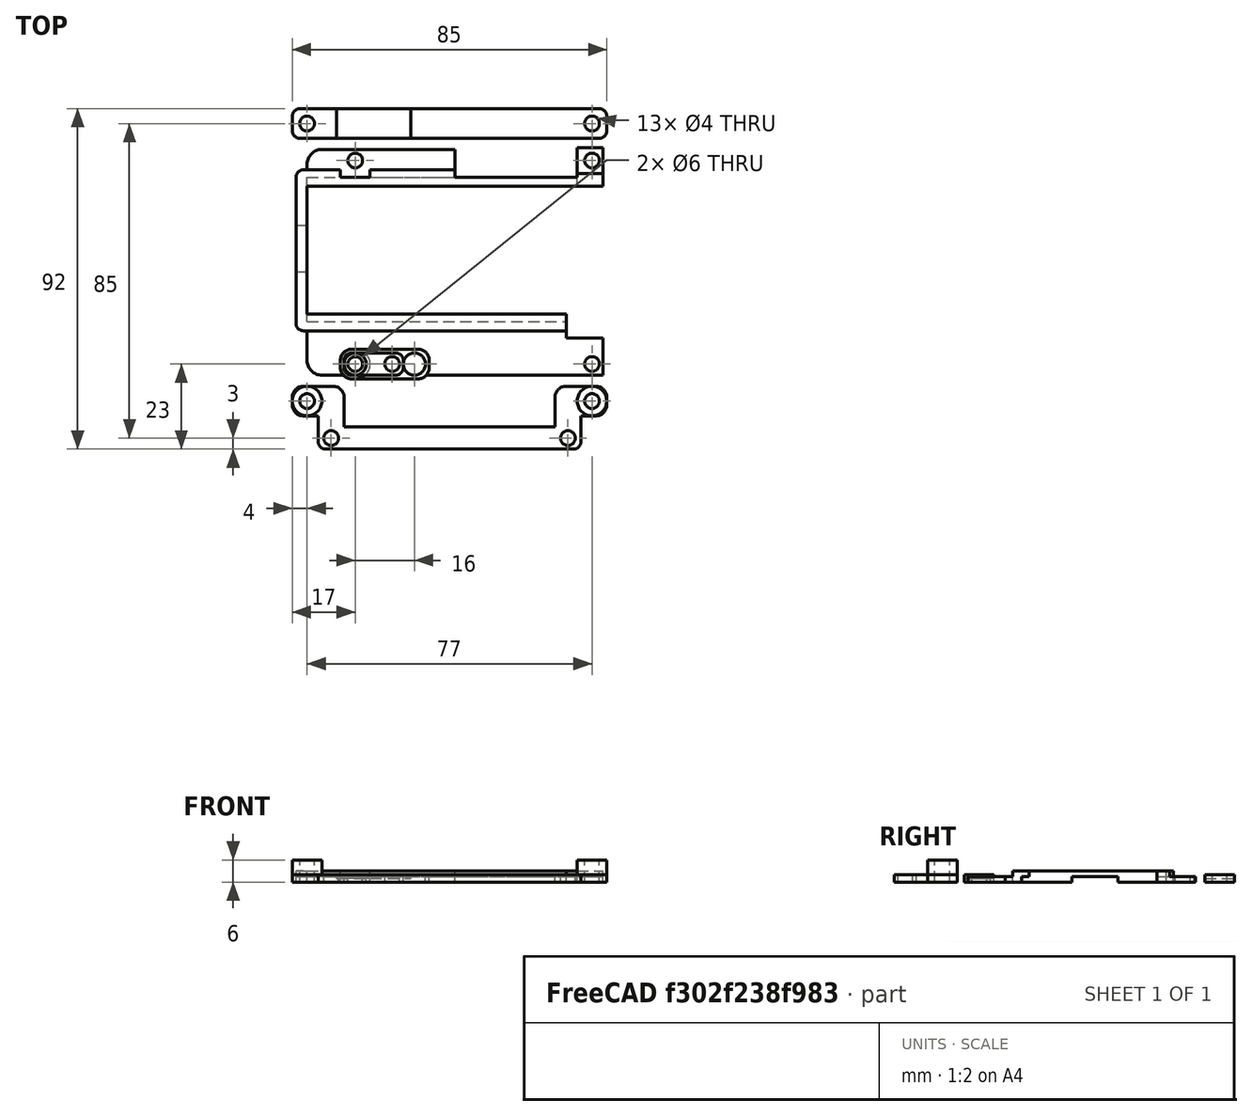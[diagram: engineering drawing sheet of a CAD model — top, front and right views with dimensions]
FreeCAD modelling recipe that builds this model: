
FCSTD DOCUMENT  (FreeCAD 0.14R3700 (Git))
Label: Parts
License: CC-BY 3.0
LicenseURL: http://creativecommons.org/licenses/by/3.0/
objects: Part::Box×21, Part::Cylinder×18, Part::Cut×17, Part::Fillet×7, Part::MultiFuse×2
note: 65 computed .brp shape members not serialized (recipe doc carries the construction recipe); baked Part::Feature solids carry a one-line shape summary decoded from their .brp

FEATURE [Part::Box] Box  label="Cube"
  Height = 2
  Length = 85
  Placement = pos=(-4,-4,0) rot=(0,0,1;0rad)
  Width = 8
FEATURE [Part::Cylinder] Cylinder001
  Angle = 360
  Height = 2
  Placement = pos=(77,0,0) rot=(0,0,1;0rad)
  Radius = 2
FEATURE [Part::Cylinder] Cylinder002
  Angle = 360
  Height = 2
  Radius = 2
FEATURE [Part::Cylinder] Cylinder
  Angle = 360
  Height = 2
  Radius = 3
FEATURE [Part::Cylinder] Cylinder003
  Angle = 360
  Height = 2
  Placement = pos=(16,0,0) rot=(0,0,1;0rad)
  Radius = 3
FEATURE [Part::Box] Box001  label="Cube001"
  Height = 2
  Length = 24
  Placement = pos=(-4,-4,0) rot=(0,0,1;0rad)
  Width = 8
FEATURE [Part::Fillet] Fillet001
  Base = -> Box001
  Edges = 4 edges r=3: [Edge1,Edge3,Edge5,Edge7]
FEATURE [Part::Cut] Cut
  Base = -> Fillet001
  Tool = -> Cylinder
FEATURE [Part::Cut] Cut004  label="Short_Part"
  Base = -> Cut
  Tool = -> Cylinder003
FEATURE [Part::Cylinder] Cylinder004
  Angle = 360
  Height = 1
  Radius = 4
FEATURE [Part::Cylinder] Cylinder005
  Angle = 360
  Height = 1
  Radius = 2
FEATURE [Part::Cylinder] Cylinder006
  Angle = 360
  Height = 2
  Placement = pos=(10,0,0) rot=(0,0,1;0rad)
  Radius = 2
FEATURE [Part::Cylinder] Cylinder007
  Angle = 360
  Height = 2
  Radius = 2
FEATURE [Part::Box] Box002  label="Cube002"
  Height = 2
  Length = 16
  Placement = pos=(-3,-3,0) rot=(0,0,1;0rad)
  Width = 6
FEATURE [Part::Box] Box003  label="Cube003"
  Height = 1
  Length = 20
  Placement = pos=(8,-4,1) rot=(0,0,1;0rad)
  Width = 8
FEATURE [Part::Cut] Cut008
  Base = -> Box
  Tool = -> Box003
FEATURE [Part::Cut] Cut009
  Base = -> Cut008
  Tool = -> Cylinder002
FEATURE [Part::Cut] Cut010
  Base = -> Cut009
  Tool = -> Cylinder001
FEATURE [Part::Fillet] Fillet  label="Long_Part"
  Base = -> Cut010
  Edges = 4 edges r=2: [Edge1,Edge3,Edge5,Edge15]
  Placement = pos=(-13,65,0) rot=(0,0,1;0rad)
FEATURE [Part::Cut] Cut011
  Base = -> Box002
  Tool = -> Cylinder007
FEATURE [Part::Cut] Cut012
  Base = -> Cut011
  Tool = -> Cylinder006
FEATURE [Part::Fillet] Fillet002  label="LCD_Holder"
  Base = -> Cut012
  Edges = 4 edges r=2: [Edge1,Edge3,Edge6,Edge13]
FEATURE [Part::Cylinder] Cylinder009
  Angle = 360
  Height = 6
  Placement = pos=(77,3,0) rot=(0,0,1;0rad)
  Radius = 2
FEATURE [Part::Cylinder] Cylinder010
  Angle = 360
  Height = 2
  Placement = pos=(6.5,-7,0) rot=(0,0,1;0rad)
  Radius = 2
FEATURE [Part::Cylinder] Cylinder011
  Angle = 360
  Height = 2
  Placement = pos=(70.5,-7,0) rot=(0,0,1;0rad)
  Radius = 2
FEATURE [Part::Box] Box004  label="Cube004"
  Height = 2
  Length = 14
  Placement = pos=(-4,-1,0) rot=(0,0,1;0rad)
  Width = 8
FEATURE [Part::Box] Box005  label="Cube005"
  Height = 2
  Length = 14
  Placement = pos=(67,-1,0) rot=(0,0,1;0rad)
  Width = 8
FEATURE [Part::Box] Box006  label="Cube006"
  Height = 2
  Length = 71
  Placement = pos=(3,-10,0) rot=(0,0,1;0rad)
  Width = 6
FEATURE [Part::Cylinder] Cylinder012
  Angle = 360
  Height = 4
  Placement = pos=(0,3,2) rot=(0,0,1;0rad)
  Radius = 4
FEATURE [Part::Cylinder] Cylinder013
  Angle = 360
  Height = 4
  Placement = pos=(77,3,2) rot=(0,0,1;0rad)
  Radius = 4
FEATURE [Part::Box] Box007  label="Cube007"
  Height = 1.5
  Length = 70
  Placement = pos=(-13,-3,0) rot=(0,0,1;0rad)
  Width = 14.5
FEATURE [Part::Cylinder] Cylinder014
  Angle = 360
  Height = 1.5
  Radius = 2
FEATURE [Part::Cylinder] Cylinder015
  Angle = 360
  Height = 1.5
  Placement = pos=(64,0,0) rot=(0,0,1;0rad)
  Radius = 2
FEATURE [Part::Box] Box008  label="Cube008"
  Height = 1.5
  Length = 70
  Placement = pos=(-13,9,1.5) rot=(0,0,1;0rad)
  Width = 4.5
FEATURE [Part::Box] Box009  label="Cube009"
  Height = 3
  Length = 3
  Placement = pos=(-16,9,0) rot=(0,0,1;0rad)
  Width = 16
FEATURE [Part::Cylinder] Cylinder016
  Angle = 360
  Height = 6
  Placement = pos=(0,3,0) rot=(0,0,1;0rad)
  Radius = 2
FEATURE [Part::Box] Box010  label="Cube010"
  Height = 2
  Length = 7
  Placement = pos=(3,-4,0) rot=(0,0,1;0rad)
  Width = 3
FEATURE [Part::Box] Box011  label="Cube011"
  Height = 2
  Length = 7
  Placement = pos=(67,-4,0) rot=(0,0,1;0rad)
  Width = 3
FEATURE [Part::MultiFuse] Fusion
  Shapes = -> [Box004,Box010,Box006,Box011,Box005,Cylinder013,Cylinder012]
FEATURE [Part::Cut] Cut020
  Base = -> Fusion
  Tool = -> Cylinder016
FEATURE [Part::Cut] Cut021
  Base = -> Cut020
  Tool = -> Cylinder011
FEATURE [Part::Cut] Cut022
  Base = -> Cut021
  Tool = -> Cylinder010
FEATURE [Part::Cut] Cut023
  Base = -> Cut022
  Tool = -> Cylinder009
FEATURE [Part::Fillet] Fillet007
  Base = -> Cut023
  Edges = 6 edges r=3: [Edge1,Edge5,Edge17,Edge73,Edge74,Edge78]
FEATURE [Part::Fillet] Fillet008  label="LCD_Holder_2"
  Base = -> Fillet007
  Edges = 2 edges r=2: [Edge52,Edge58]
  Placement = pos=(-13,-13,0) rot=(0,0,1;0rad)
FEATURE [Part::Box] Box012  label="Cube012"
  Height = 1.5
  Length = 10
  Placement = pos=(57,-3,0) rot=(0,0,1;0rad)
  Width = 10
FEATURE [Part::Cut] Cut026  label="Washer"
  Base = -> Cylinder004
  Tool = -> Cylinder005
FEATURE [Part::Cylinder] Cylinder017
  Angle = 360
  Height = 1.5
  Placement = pos=(64,55,0) rot=(0,0,1;0rad)
  Radius = 2
FEATURE [Part::Cylinder] Cylinder018
  Angle = 360
  Height = 1.5
  Placement = pos=(0,55,0) rot=(0,0,1;0rad)
  Radius = 2
FEATURE [Part::Box] Box013  label="Cube013"
  Height = 1.5
  Length = 40
  Placement = pos=(-13,50.5,0) rot=(0,0,1;0rad)
  Width = 7.5
FEATURE [Part::Box] Box014  label="Cube014"
  Height = 1.5
  Length = 3
  Placement = pos=(-16,25,1.5) rot=(0,0,1;0rad)
  Width = 12.5
FEATURE [Part::Box] Box015  label="Cube015"
  Height = 1.5
  Length = 7
  Placement = pos=(60,48,0) rot=(0,0,1;0rad)
  Width = 10.5
FEATURE [Part::Box] Box016  label="Cube016"
  Height = 1.5
  Length = 40
  Placement = pos=(-13,48,1.5) rot=(0,0,1;0rad)
  Width = 4.5
FEATURE [Part::Box] Box017  label="Cube017"
  Height = 3
  Length = 3
  Placement = pos=(-16,37.5,0) rot=(0,0,1;0rad)
  Width = 15
FEATURE [Part::Box] Box018  label="Cube018"
  Height = 1.5
  Length = 33
  Placement = pos=(27,48,1.5) rot=(0,0,1;0rad)
  Width = 2.5
FEATURE [Part::Box] Box019  label="Cube019"
  Height = 1.5
  Length = 7
  Placement = pos=(60,48,1.5) rot=(0,0,1;0rad)
  Width = 3.5
FEATURE [Part::Box] Box020  label="Cube020"
  Height = 1.5
  Length = 8
  Placement = pos=(-4,50.5,1.5) rot=(0,0,1;0rad)
  Width = 2
FEATURE [Part::MultiFuse] Fusion001
  Shapes = -> [Box012,Box007,Box008,Box009,Box014,Box017,Box016,Box013,Box018,Box019,Box015]
FEATURE [Part::Cut] Cut027
  Base = -> Fusion001
  Tool = -> Box020
FEATURE [Part::Cut] Cut028
  Base = -> Cut027
  Tool = -> Cylinder018
FEATURE [Part::Cut] Cut029
  Base = -> Cut028
  Tool = -> Cylinder017
FEATURE [Part::Cut] Cut030
  Base = -> Cut029
  Tool = -> Cylinder015
FEATURE [Part::Cut] Cut031
  Base = -> Cut030
  Tool = -> Cylinder014
FEATURE [Part::Fillet] Fillet009
  Base = -> Cut031
  Edges = 2 edges r=4: [Edge16,Edge115]
FEATURE [Part::Fillet] Fillet010  label="Board_Holder"
  Base = -> Fillet009
  Edges = 2 edges r=2: [Edge43,Edge72]
